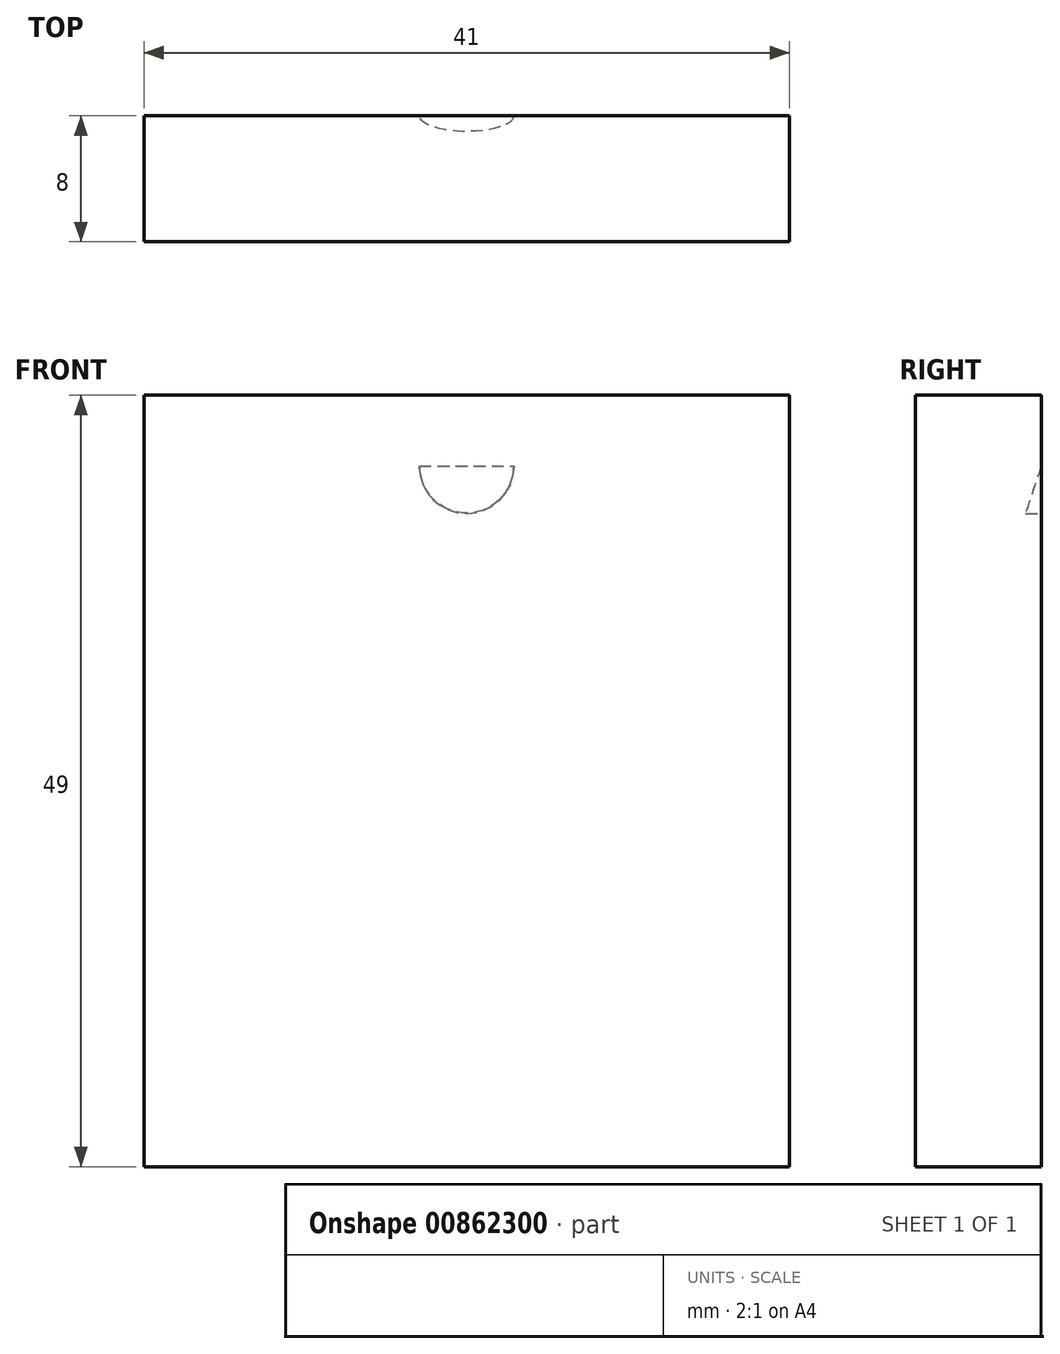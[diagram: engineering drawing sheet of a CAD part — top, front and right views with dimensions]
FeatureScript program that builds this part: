
annotation { "Feature Type Name" : "Feature", "Feature Type Description" : "" }
export const myFeature = defineFeature(function(context is Context, id is Id, definition is map)
    precondition{}
    {
        {
            var Q0;
            Q0=qCreatedBy(makeId("Front.planeOp"),FACE);
            var sketch = newSketch(context, id + "F0", { "sketchPlane" : qUnion([Q0])});
            skLineSegment(sketch, "E0.bottom", {"start": v(-20.5, 24.5) * mm, "end": v(20.5, 24.5) * mm});
            skLineSegment(sketch, "E0.top", {"start": v(-20.5, -24.5) * mm, "end": v(20.5, -24.5) * mm});
            skLineSegment(sketch, "E0.left", {"start": v(-20.5, 24.5) * mm, "end": v(-20.5, -24.5) * mm});
            skLineSegment(sketch, "E0.right", {"start": v(20.5, 24.5) * mm, "end": v(20.5, -24.5) * mm});
            skPoint(sketch, "E0.middle", {"position": v(0, 0) * mm});
            skSolve(sketch);
        }
        {
            var Q0;
            Q0 = qSketchRegion(id + "F0", true);
            extrude(context, id + "F1", {"entities" : qUnion([Q0]), "depth" : 8 * mm, "offsetDistance" : 25 * mm});
        }
        {
            var Q0;
            Q0=qCreatedBy(makeId("Front.planeOp"),FACE);
            var sketch = newSketch(context, id + "F2", { "sketchPlane" : qUnion([Q0])});
            skLineSegment(sketch, "E1", {"start": v(0, 0) * mm, "end": v(0, 20) * mm, "construction": true});
            skArc(sketch, "E2", {"start": v(-3, 20) * mm, "mid": v(0, 17) * mm, "end": v(3, 20) * mm});
            skLineSegment(sketch, "E3", {"start": v(-3, 20) * mm, "end": v(3, 20) * mm});
            skSolve(sketch);
        }
        {
            var Q0;
            Q0 = qSketchRegion(id + "F2", true);
            extrude(context, id + "F3", {"entities" : qUnion([Q0]), "operationType" : NewBodyOperationType.REMOVE, "depth" : 1 * mm, "offsetDistance" : 25 * mm});
        }
        {
            var Q0;
            Q0=makeQuery(id+"F3.boolean.opBoolean","COPY",EDGE,{"derivedFrom":makeQuery(id+"F3.opExtrude","CAP_EDGE",EDGE,{"disambiguationData":[OSD([sQuery(id+"F2.wireOp",EDGE,"E3")])],"isStart":false})});
            chamfer(context, id + "F4", {"entities" : qUnion([Q0]), "chamferType" : ChamferType.TWO_OFFSETS, "width1" : 1 * mm, "oppositeDirection" : true, "width2" : 3 * mm, "tangentPropagation" : true});
        }
    });
